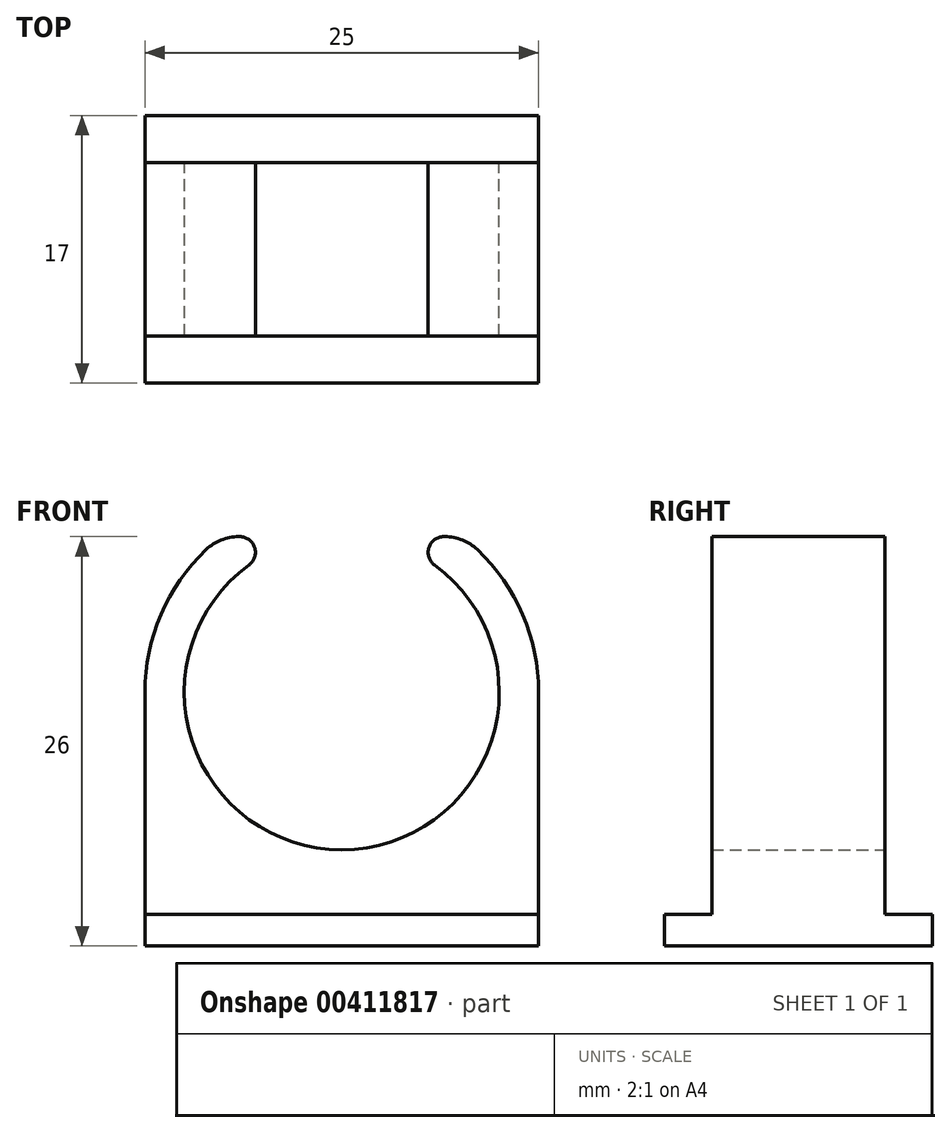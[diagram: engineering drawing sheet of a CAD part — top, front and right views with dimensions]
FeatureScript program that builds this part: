
annotation { "Feature Type Name" : "Feature", "Feature Type Description" : "" }
export const myFeature = defineFeature(function(context is Context, id is Id, definition is map)
    precondition{}
    {
        {
            var Q0;
            Q0=qCreatedBy(makeId("Front.planeOp"),FACE);
            var sketch = newSketch(context, id + "F0", { "sketchPlane" : qUnion([Q0])});
            skLineSegment(sketch, "E0.bottom", {"start": v(0, 0) * mm, "end": v(25, 0) * mm});
            skLineSegment(sketch, "E0.top", {"start": v(5.95, 24) * mm, "end": v(6.01, 24) * mm});
            skLineSegment(sketch, "E0.left", {"start": v(0, 0) * mm, "end": v(0, 14.12) * mm});
            skLineSegment(sketch, "E0.right", {"start": v(25, 0) * mm, "end": v(25, 14.12) * mm});
            skArc(sketch, "E1", {"start": v(6.6, 22.2) * mm, "mid": v(12.5, 4.12) * mm, "end": v(18.4, 22.2) * mm});
            skPoint(sketch, "E1.centerSnap0", {"position": v(12.5, 24) * mm});
            skArc(sketch, "E2", {"start": v(3.88, 23.17) * mm, "mid": v(1.01, 19.04) * mm, "end": v(0, 14.12) * mm});
            skArc(sketch, "E3.trimOffspring", {"start": v(25, 14.12) * mm, "mid": v(23.99, 19.04) * mm, "end": v(21.12, 23.17) * mm});
            skPoint(sketch, "E4.orphan", {"position": v(0, 24) * mm});
            skLineSegment(sketch, "E5.trimOffspring", {"start": v(18.99, 24) * mm, "end": v(19.05, 24) * mm});
            skPoint(sketch, "E6.orphan", {"position": v(25, 24) * mm});
            skPoint(sketch, "E7.visualSharp", {"position": v(10.97, 24) * mm});
            skArc(sketch, "E7.filletArc", {"start": v(6.6, 22.2) * mm, "mid": v(6.96, 23.31) * mm, "end": v(6.01, 24) * mm});
            skPoint(sketch, "E8.visualSharp", {"position": v(14.03, 24) * mm});
            skArc(sketch, "E8.filletArc", {"start": v(18.99, 24) * mm, "mid": v(18.04, 23.31) * mm, "end": v(18.4, 22.2) * mm});
            skPoint(sketch, "E9.visualSharp", {"position": v(4.85, 24) * mm});
            skArc(sketch, "E9.filletArc", {"start": v(5.95, 24) * mm, "mid": v(4.84, 23.79) * mm, "end": v(3.88, 23.17) * mm});
            skPoint(sketch, "E10.visualSharp", {"position": v(20.15, 24) * mm});
            skArc(sketch, "E10.filletArc", {"start": v(21.12, 23.17) * mm, "mid": v(20.16, 23.79) * mm, "end": v(19.05, 24) * mm});
            skSolve(sketch);
        }
        {
            var Q0;
            Q0 = qSketchRegion(id + "F0", true);
            extrude(context, id + "F1", {"entities" : qUnion([Q0]), "depth" : 11 * mm});
        }
        {
            var Q0;
            Q0=makeQuery(id+"F1.opExtrude","SWEPT_FACE",FACE,{"disambiguationData":[OSD([sQuery(id+"F0.wireOp",EDGE,"E0.bottom")])]});
            var sketch = newSketch(context, id + "F2", { "sketchPlane" : qUnion([Q0])});
            skLineSegment(sketch, "E11.bottom", {"start": v(0, 14) * mm, "end": v(25, 14) * mm});
            skLineSegment(sketch, "E11.top", {"start": v(0, -3) * mm, "end": v(25, -3) * mm});
            skLineSegment(sketch, "E11.left", {"start": v(0, 14) * mm, "end": v(0, -3) * mm});
            skLineSegment(sketch, "E11.right", {"start": v(25, 14) * mm, "end": v(25, -3) * mm});
            skSolve(sketch);
        }
        {
            var Q0;
            Q0 = qSketchRegion(id + "F2", true);
            extrude(context, id + "F3", {"entities" : qUnion([Q0]), "operationType" : NewBodyOperationType.ADD, "depth" : 2 * mm});
        }
    });
